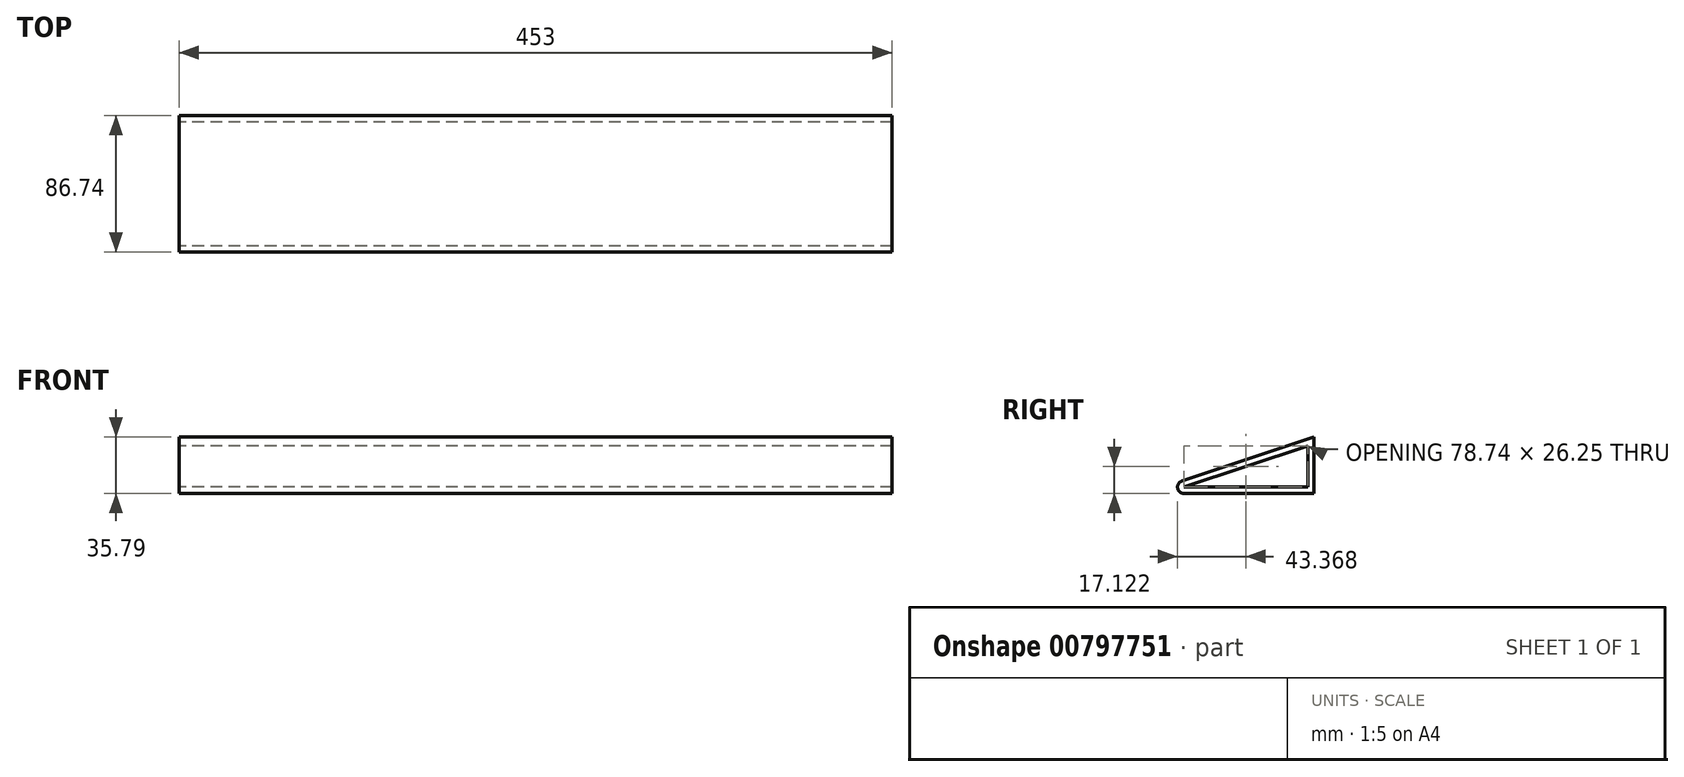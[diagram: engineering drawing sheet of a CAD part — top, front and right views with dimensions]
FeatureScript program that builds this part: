
annotation { "Feature Type Name" : "Feature", "Feature Type Description" : "" }
export const myFeature = defineFeature(function(context is Context, id is Id, definition is map)
    precondition{}
    {
        {
            var Q0;
            Q0=qCreatedBy(makeId("Right.planeOp"),FACE);
            var sketch = newSketch(context, id + "F0", { "sketchPlane" : qUnion([Q0])});
            skLineSegment(sketch, "E0", {"start": v(0, 0) * mm, "end": v(0, 80) * mm, "construction": true});
            skLineSegment(sketch, "E1", {"start": v(0, 80) * mm, "end": v(-54, 80) * mm, "construction": true});
            skLineSegment(sketch, "E2", {"start": v(-54, 80) * mm, "end": v(-54, 70) * mm, "construction": true});
            skLineSegment(sketch, "E3", {"start": v(-168, 32) * mm, "end": v(-168, 0) * mm, "construction": true});
            skLineSegment(sketch, "E4", {"start": v(-168, 0) * mm, "end": v(0, 0) * mm, "construction": true});
            skLineSegment(sketch, "E5", {"start": v(-54.16, 69.95) * mm, "end": v(-55.42, 73.74) * mm, "construction": true});
            skLineSegment(sketch, "E6", {"start": v(-55.42, 73.74) * mm, "end": v(-169.26, 35.8) * mm, "construction": true});
            skLineSegment(sketch, "E7", {"start": v(-169.26, 35.8) * mm, "end": v(-168, 32) * mm, "construction": true});
            skLineSegment(sketch, "E8", {"start": v(-168, 32) * mm, "end": v(-54.16, 69.95) * mm, "construction": true});
            skLineSegment(sketch, "E9.bottom", {"start": v(-169.26, 0) * mm, "end": v(-252, 0) * mm});
            skLineSegment(sketch, "E9.left", {"start": v(-169.26, 0) * mm, "end": v(-169.26, 35.8) * mm});
            skLineSegment(sketch, "E10", {"start": v(-169.26, 35.8) * mm, "end": v(-253.26, 7.8) * mm});
            skPoint(sketch, "E11.visualSharp", {"position": v(-276.65, 0) * mm});
            skArc(sketch, "E11.filletArc", {"start": v(-253.26, 7.8) * mm, "mid": v(-255.95, 3.36) * mm, "end": v(-252, 0) * mm});
            skLineSegment(sketch, "E12.0", {"start": v(-173.26, 30.25) * mm, "end": v(-252, 4) * mm});
            skLineSegment(sketch, "E12.1", {"start": v(-173.26, 4) * mm, "end": v(-173.26, 30.25) * mm});
            skLineSegment(sketch, "E12.2", {"start": v(-173.26, 4) * mm, "end": v(-252, 4) * mm});
            skSolve(sketch);
        }
        {
            var Q0;
            Q0 = qSketchRegion(id + "F0", true);
            extrude(context, id + "F1", {"entities" : qUnion([Q0]), "depth" : 453 * mm, "offsetDistance" : 25 * mm});
        }
    });
